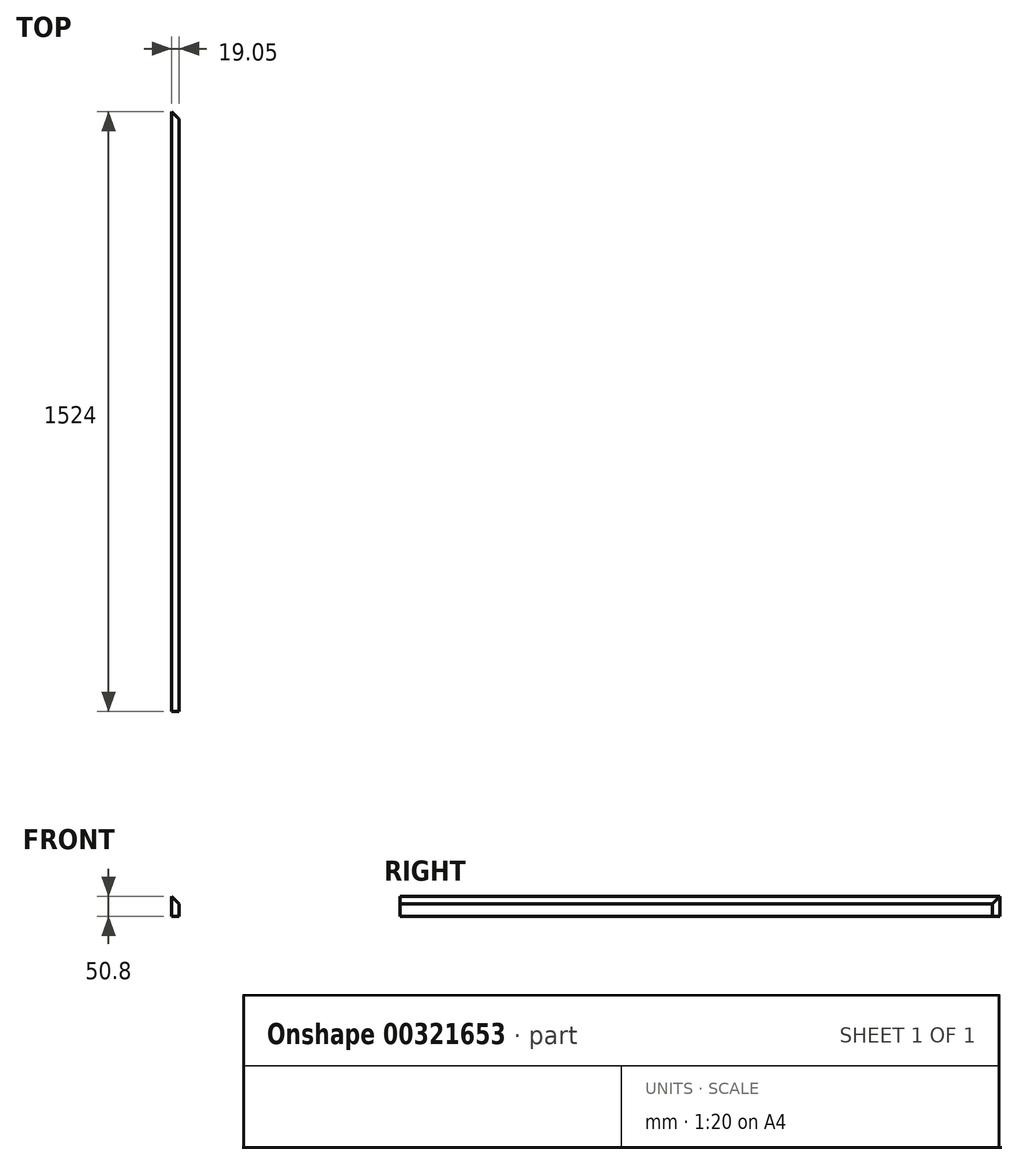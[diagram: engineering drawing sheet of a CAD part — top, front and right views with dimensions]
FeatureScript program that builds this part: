
annotation { "Feature Type Name" : "Feature", "Feature Type Description" : "" }
export const myFeature = defineFeature(function(context is Context, id is Id, definition is map)
    precondition{}
    {
        {
            var Q0;
            Q0=qCreatedBy(makeId("Right.planeOp"),FACE);
            var sketch = newSketch(context, id + "F0", { "sketchPlane" : qUnion([Q0])});
            skLineSegment(sketch, "E0.bottom", {"start": v(762, 25.4) * mm, "end": v(-762, 25.4) * mm});
            skLineSegment(sketch, "E0.top", {"start": v(762, -25.4) * mm, "end": v(-762, -25.4) * mm});
            skLineSegment(sketch, "E0.left", {"start": v(762, 25.4) * mm, "end": v(762, -25.4) * mm});
            skLineSegment(sketch, "E0.right", {"start": v(-762, 25.4) * mm, "end": v(-762, -25.4) * mm});
            skPoint(sketch, "E0.middle", {"position": v(0, 0) * mm});
            skSolve(sketch);
        }
        {
            var Q0;
            Q0 = qSketchRegion(id + "F0", true);
            extrude(context, id + "F1", {"entities" : qUnion([Q0]), "depth" : 19.05 * mm});
        }
        {
            var Q0;
            Q0=makeQuery(id+"F1.opExtrude","SWEPT_FACE",FACE,{"disambiguationData":[OSD([sQuery(id+"F0.wireOp",EDGE,"E0.bottom")])]});
            var sketch = newSketch(context, id + "F2", { "sketchPlane" : qUnion([Q0])});
            skLineSegment(sketch, "E1", {"start": v(0, 762) * mm, "end": v(19.05, 762) * mm});
            skLineSegment(sketch, "E2", {"start": v(19.05, 762) * mm, "end": v(19.05, 742.95) * mm});
            skLineSegment(sketch, "E3", {"start": v(19.05, 742.95) * mm, "end": v(0, 762) * mm});
            skSolve(sketch);
        }
        {
            var Q0;
            Q0=makeQuery(id+"F2.imprint","IMPRINT",FACE,{"disambiguationData":[TD([[makeQuery(id+"F2.imprint","IMPRINT",EDGE,{"derivedFrom":sQuery(id+"F2.wireOp",EDGE,"E1")}),1.0]])]});
            extrude(context, id + "F3", {"entities" : qUnion([Q0]), "operationType" : NewBodyOperationType.REMOVE, "endBound" : BoundingType.THROUGH_ALL, "oppositeDirection" : true, "depth" : 25.4 * mm});
        }
        {
            var Q0;
            Q0=makeQuery(id+"F1.opExtrude","SWEPT_FACE",FACE,{"disambiguationData":[OSD([sQuery(id+"F0.wireOp",EDGE,"E0.right")])]});
            var sketch = newSketch(context, id + "F4", { "sketchPlane" : qUnion([Q0])});
            skLineSegment(sketch, "E4", {"start": v(0, 25.4) * mm, "end": v(19.05, 25.4) * mm});
            skLineSegment(sketch, "E5", {"start": v(19.05, 25.4) * mm, "end": v(19.05, 6.35) * mm});
            skLineSegment(sketch, "E6", {"start": v(19.05, 6.35) * mm, "end": v(0, 25.4) * mm});
            skSolve(sketch);
        }
        {
            var Q0;
            Q0=makeQuery(id+"F4.imprint","IMPRINT",FACE,{"disambiguationData":[TD([[makeQuery(id+"F4.imprint","IMPRINT",EDGE,{"derivedFrom":sQuery(id+"F4.wireOp",EDGE,"E4")}),1.0]])]});
            extrude(context, id + "F5", {"entities" : qUnion([Q0]), "operationType" : NewBodyOperationType.REMOVE, "endBound" : BoundingType.THROUGH_ALL, "oppositeDirection" : true, "depth" : 25.4 * mm});
        }
    });
